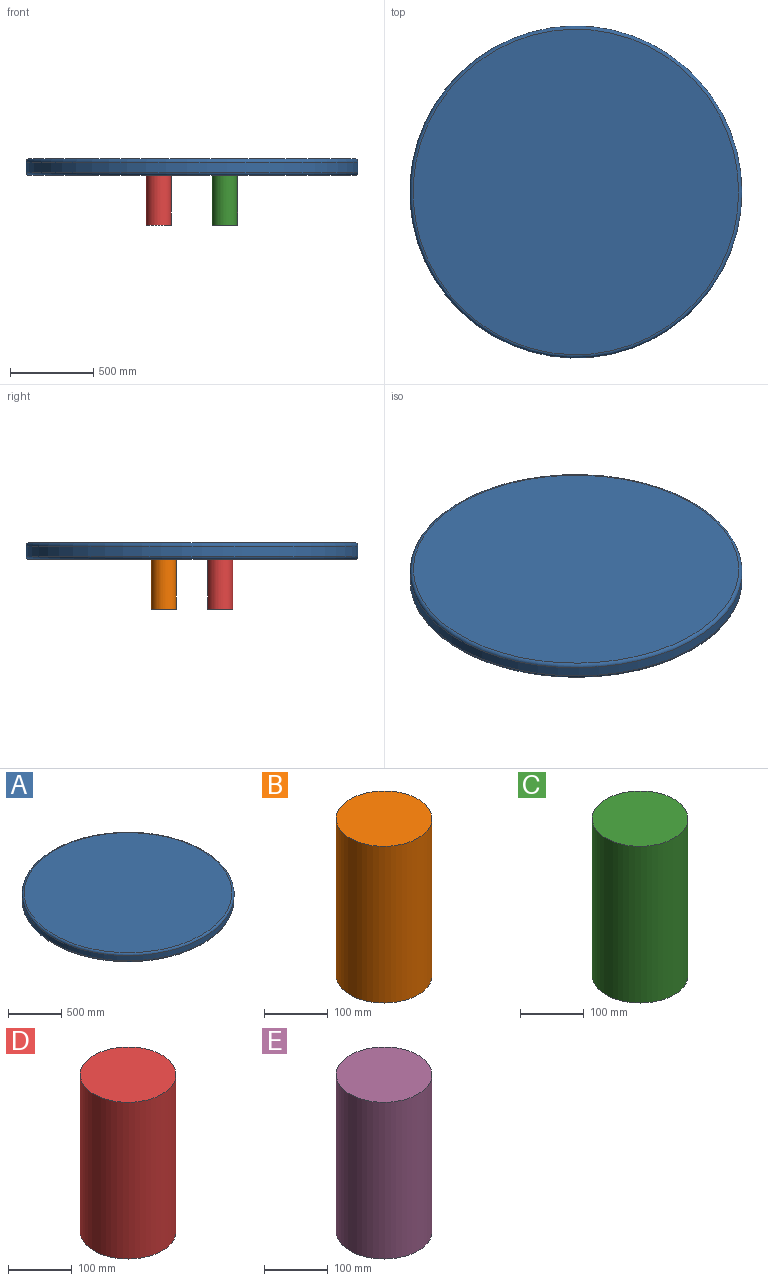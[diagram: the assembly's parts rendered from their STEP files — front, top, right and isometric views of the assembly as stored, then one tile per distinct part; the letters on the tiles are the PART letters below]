
ASSEMBLY  parts=5 mates=4
PART A: 5 faces, bbox 2164.8x2164.8x100 mm
  f0: cylinder r=1000mm len=2000mm, axis (0,0,-1), area 376991.1mm2, adj f3,f4
  f1: plane 1960x1960mm, normal (0,0,1), area 3017185.6mm2, adj f4
  f2: plane 1960x1960mm, normal (0,0,-1), area 3017185.6mm2, adj f3
  f3: torus R=980mm, axis (0,0,1), area 195957.5mm2, adj f0,f2
  f4: torus R=980mm, axis (0,0,1), area 195957.5mm2, adj f0,f1
PART B: 3 faces, bbox 150x150x300 mm
  f0: cylinder r=75mm len=300mm, axis (0,0,1), area 141371.7mm2, adj f1,f2
  f1: plane 150x150mm, normal (0,0,-1), area 17671.5mm2, adj f0
  f2: plane 150x150mm, normal (0,0,1), area 17671.5mm2, adj f0
PART C: 3 faces, bbox 150x150x300 mm
  f0: cylinder r=75mm len=300mm, axis (0,0,1), area 141371.7mm2, adj f1,f2
  f1: plane 150x150mm, normal (0,0,-1), area 17671.5mm2, adj f0
  f2: plane 150x150mm, normal (0,0,1), area 17671.5mm2, adj f0
PART D: 3 faces, bbox 150x150x300 mm
  f0: cylinder r=75mm len=300mm, axis (0,0,1), area 141371.7mm2, adj f1,f2
  f1: plane 150x150mm, normal (0,0,-1), area 17671.5mm2, adj f0
  f2: plane 150x150mm, normal (0,0,1), area 17671.5mm2, adj f0
PART E: 3 faces, bbox 150x150x300 mm
  f0: cylinder r=75mm len=300mm, axis (0,0,1), area 141371.7mm2, adj f1,f2
  f1: plane 150x150mm, normal (0,0,-1), area 17671.5mm2, adj f0
  f2: plane 150x150mm, normal (0,0,1), area 17671.5mm2, adj f0
PLACE A t=(-379.08,-153.68,91.67)mm
PLACE B t=(-179.08,-266.68,91.67)mm
PLACE C t=(-582.08,-153.68,91.67)mm
PLACE D t=(-179.08,-153.68,91.67)mm
PLACE E t=(-579.08,-266.68,91.67)mm
MATE fastened B.f0 <-> A.f2  axis (0,0,1) through (-579.08,16.32,91.67)mm
MATE fastened A.f2 <-> E.f0  axis (0,0,-1) through (-179.08,16.32,91.67)mm
MATE fastened A.f2 <-> D.f0  axis (0,0,-1) through (-579.08,-323.68,91.67)mm
MATE fastened C.f0 <-> A.f2  axis (0,0,1) through (-182.08,-323.68,91.67)mm
